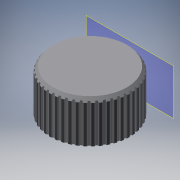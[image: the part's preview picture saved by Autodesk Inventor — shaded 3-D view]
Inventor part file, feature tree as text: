
AUTODESK INVENTOR PART (.ipt)
format: ipt  version: 2018 (Build 220112000, 112)  size: 710,656 bytes
history: native  units: mm
features: extrude x4, sketch x4, chamfer x3, fillet x2, reference x2, other x2, plane x1, pattern_circular x1
ambient origin geometry x8: Origin, YZ Plane, XZ Plane, XY Plane, X Axis, Y Axis, Z Axis, Center Point
bodies: Volumenkörper1 (feature_tree)
feature tree (19):
  extrude  "Extrusion1"  Depth=16.0mm TaperAngle=0.0deg
  extrude  "Extrusion2"  Depth=1.0mm
  extrude  "Extrusion3"  TaperAngle=360.0deg  [1 undecoded]
  plane  "Arbeitsebene1"
  sketch  "Skizze4"  dims[d9=1.0mm d10=1.5mm d11=2.0mm d12=45.0deg d13=0.5mm d14=0.0mm d15=450.0mm d16=360.0deg d21=0.25mm d22=2.0mm d23=45.0deg d24=0.25mm d25=7.0mm d26=16.0mm d27=45.0deg d28=17.75mm]
  chamfer  "Fase1"  Distance=1.5mm Angle=45.0deg
  extrude  "Extrusion4"  Depth=17.75mm TaperAngle=0.0deg
  chamfer  "Fase3"  Distance=450.0mm Angle=360.0deg
  fillet  "Rundung1"  Radius=0.25mm
  pattern_circular  "Runde Anordnung1"  [2 undecoded]
  chamfer  "Fase4"  Distance=16.0mm Angle=45.0deg
  fillet  "Rundung2"  Radius=17.75mm
  sketch  "Skizze1"  dims[d0=0.05mm d1=16.0mm d2=0.0mm]
  reference  "Referenz1"
  reference  "Referenz2"
  sketch  "Skizze2"  dims[d3=1.0mm d4=0.0mm d5=1.0mm]
  sketch  "Skizze3"  dims[d6=20.0mm d7=0.0mm d8=360.0deg]
  parser-record x1  (decoder bookkeeping rows leaked as tree rows — omitted from the tree; the rows remain in map.json)
  other  "VolumeKnob.iam"
note: 3 required parameter values undecoded (feature->parameter linkage not recoverable at this tier; creation-order binding heuristic only, values carry confidence <= 0.55)
note: 1 file-system path scrubbed to <path> (originals preserved in map.json)
